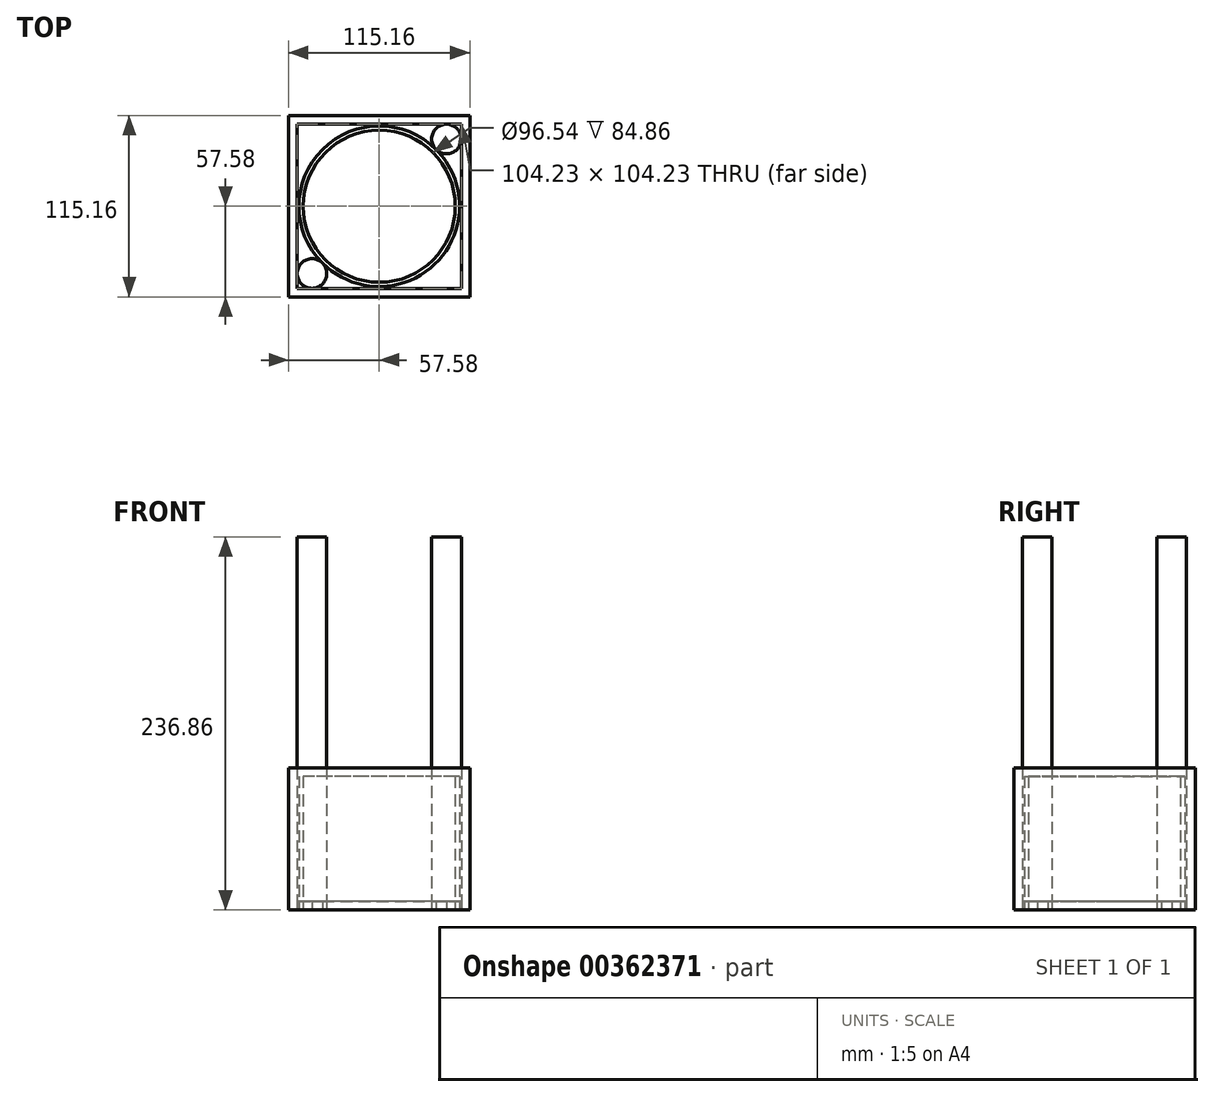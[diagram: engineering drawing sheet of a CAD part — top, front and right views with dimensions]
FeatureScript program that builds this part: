
annotation { "Feature Type Name" : "Feature", "Feature Type Description" : "" }
export const myFeature = defineFeature(function(context is Context, id is Id, definition is map)
    precondition{}
    {
        {
            var Q0;
            Q0=qCreatedBy(makeId("Top.planeOp"),FACE);
            var sketch = newSketch(context, id + "F0", { "sketchPlane" : qUnion([Q0])});
            skLineSegment(sketch, "E0.bottom", {"start": v(57.57, 57.58) * mm, "end": v(-57.58, 57.58) * mm});
            skLineSegment(sketch, "E0.top", {"start": v(57.58, -57.58) * mm, "end": v(-57.57, -57.58) * mm});
            skLineSegment(sketch, "E0.left", {"start": v(57.57, 57.58) * mm, "end": v(57.58, -57.58) * mm});
            skLineSegment(sketch, "E0.right", {"start": v(-57.58, 57.58) * mm, "end": v(-57.57, -57.58) * mm});
            skPoint(sketch, "E0.middle", {"position": v(0, 0) * mm});
            skLineSegment(sketch, "E1.bottom", {"start": v(52.11, 52.12) * mm, "end": v(-52.12, 52.12) * mm});
            skLineSegment(sketch, "E1.top", {"start": v(52.12, -52.12) * mm, "end": v(-52.11, -52.12) * mm});
            skLineSegment(sketch, "E1.left", {"start": v(52.11, 52.12) * mm, "end": v(52.12, -52.11) * mm});
            skLineSegment(sketch, "E1.right", {"start": v(-52.12, 52.11) * mm, "end": v(-52.11, -52.12) * mm});
            skCircle(sketch, "E2", {"center": v(-42.72, -42.72) * mm, "radius": 9.4 * mm});
            skCircle(sketch, "E3.MirrorC", {"center": v(42.72, 42.72) * mm, "radius": 9.4 * mm});
            skCircle(sketch, "E4", {"center": v(0, 0) * mm, "radius": 51.02 * mm});
            skCircle(sketch, "E5", {"center": v(0, 0) * mm, "radius": 48.27 * mm});
            skSolve(sketch);
        }
        {
            var Q0;
            Q0 = qSketchRegion(id + "F0", true);
            extrude(context, id + "F1", {"entities" : qUnion([Q0]), "depth" : 90.26 * mm});
        }
        {
            var Q0;
            {var subQ0=sQuery(id+"F0.wireOp",EDGE,"E3.MirrorC");var subQ1=makeQuery(id+"F0.imprint","INTERSECT",VERTEX,{"derivedFrom":[sQuery(id+"F0.wireOp",EDGE,"E1.bottom"),subQ0]});Q0=makeQuery(id+"F0.imprint","IMPRINT",FACE,{"disambiguationData":[TD([[makeQuery(id+"F0.imprint","IMPRINT",EDGE,{"disambiguationData":[TD([[subQ1,1.0]])],"derivedFrom":subQ0}),1.0]])]});}
            var Q1;
            {var subQ0=sQuery(id+"F0.wireOp",EDGE,"E2");var subQ1=makeQuery(id+"F0.imprint","INTERSECT",VERTEX,{"derivedFrom":[sQuery(id+"F0.wireOp",EDGE,"E1.top"),subQ0]});Q1=makeQuery(id+"F0.imprint","IMPRINT",FACE,{"disambiguationData":[TD([[makeQuery(id+"F0.imprint","IMPRINT",EDGE,{"disambiguationData":[TD([[subQ1,1.0]])],"derivedFrom":subQ0}),1.0]])]});}
            extrude(context, id + "F2", {"entities" : qUnion([Q0, Q1]), "depth" : 236.86 * mm});
        }
        {
            var Q0;
            {var subQ7=sQuery(id+"F0.wireOp",EDGE,"E1.right");var subQ8=sQuery(id+"F0.wireOp",EDGE,"E1.bottom");var subQ9=makeQuery(id+"F0.imprint","INTERSECT",VERTEX,{"derivedFrom":[subQ8,subQ7]});Q0=makeQuery(id+"F0.imprint","IMPRINT",FACE,{"disambiguationData":[TD([[makeQuery(id+"F0.imprint","IMPRINT",EDGE,{"disambiguationData":[TD([[subQ9,1.0]])],"derivedFrom":subQ8}),1.0]])]});}
            var Q1;
            {var subQ0=sQuery(id+"F0.wireOp",EDGE,"E1.left");var subQ1=sQuery(id+"F0.wireOp",EDGE,"E1.bottom");var subQ2=makeQuery(id+"F0.imprint","INTERSECT",VERTEX,{"derivedFrom":[subQ1,subQ0]});Q1=makeQuery(id+"F0.imprint","IMPRINT",FACE,{"disambiguationData":[TD([[makeQuery(id+"F0.imprint","IMPRINT",EDGE,{"disambiguationData":[TD([[subQ2,-1.0]])],"derivedFrom":subQ1}),1.0]])]});}
            var Q2;
            {var subQ0=sQuery(id+"F0.wireOp",EDGE,"E1.right");var subQ1=sQuery(id+"F0.wireOp",EDGE,"E1.top");var subQ2=makeQuery(id+"F0.imprint","INTERSECT",VERTEX,{"derivedFrom":[subQ1,subQ0]});Q2=makeQuery(id+"F0.imprint","IMPRINT",FACE,{"disambiguationData":[TD([[makeQuery(id+"F0.imprint","IMPRINT",EDGE,{"disambiguationData":[TD([[subQ2,1.0]])],"derivedFrom":subQ1}),-1.0]])]});}
            var Q3;
            {var subQ1=sQuery(id+"F0.wireOp",EDGE,"E1.left");var subQ6=sQuery(id+"F0.wireOp",EDGE,"E1.top");var subQ9=makeQuery(id+"F0.imprint","INTERSECT",VERTEX,{"derivedFrom":[subQ6,subQ1]});Q3=makeQuery(id+"F0.imprint","IMPRINT",FACE,{"disambiguationData":[TD([[makeQuery(id+"F0.imprint","IMPRINT",EDGE,{"disambiguationData":[TD([[subQ9,-1.0]])],"derivedFrom":subQ6}),-1.0]])]});}
            var Q4;
            Q4=makeQuery(id+"F0.imprint","IMPRINT",FACE,{"disambiguationData":[TD([[makeQuery(id+"F0.imprint","IMPRINT",EDGE,{"derivedFrom":sQuery(id+"F0.wireOp",EDGE,"E5")}),1.0]])]});
            extrude(context, id + "F3", {"entities" : qUnion([Q0, Q1, Q2, Q3, Q4]), "depth" : 5.46 * mm});
        }
        {
            var Q0;
            Q0=makeQuery(id+"F0.imprint","IMPRINT",FACE,{"disambiguationData":[TD([[makeQuery(id+"F0.imprint","IMPRINT",EDGE,{"derivedFrom":sQuery(id+"F0.wireOp",EDGE,"E5")}),-1.0]])]});
            extrude(context, id + "F4", {"entities" : qUnion([Q0]), "depth" : 84.86 * mm});
        }
    });
